# Revit family: isFang, isolierter Fangmast
name_source: partatom
category: Generic Models
revit_build: Autodesk Revit 2015 (Build: 20140606_1530(x64)
units: mm (PartAtom-declared; Revit-internal decimal feet)

## types (4) — shared parameters
Height 1 = 1560 mm  [stored 5.11811 ft]
Height 2 = 865 mm  [stored 2.83793 ft]
Manufacturer = OBO Bettermann
URL = http://www.obo-bettermann.com

## per-type parameters (varying)
| type | GTIN | Height | Manufacturer Art.No. | Material |
| isFang 4000 AL | 4012195785330 | 1440 mm  [stored 4.72441 ft] | 5408943 | Aluminum |
| isFang 6000 AL | 4012195785347 | 3440 mm  [stored 11.2861 ft] | 5408947 | Aluminum |
| isFang 4000 | 4012195670056 | 1440 mm  [stored 4.72441 ft] | 5408942 | Fibre-glass-reinforced plastic |
| isFang 6000 | 4012195670063 | 3440 mm  [stored 11.2861 ft] | 5408946 | Fibre-glass-reinforced plastic |

note: column(s) folded — value = type name in every type: Article Type

note: [stored X ft] marks values corroborated as IEEE doubles in the binary element streams (Revit-internal decimal feet)

## geometry (parser evidence)
native form markers: Sweep x2
no freeform markers — native parametric forms only
